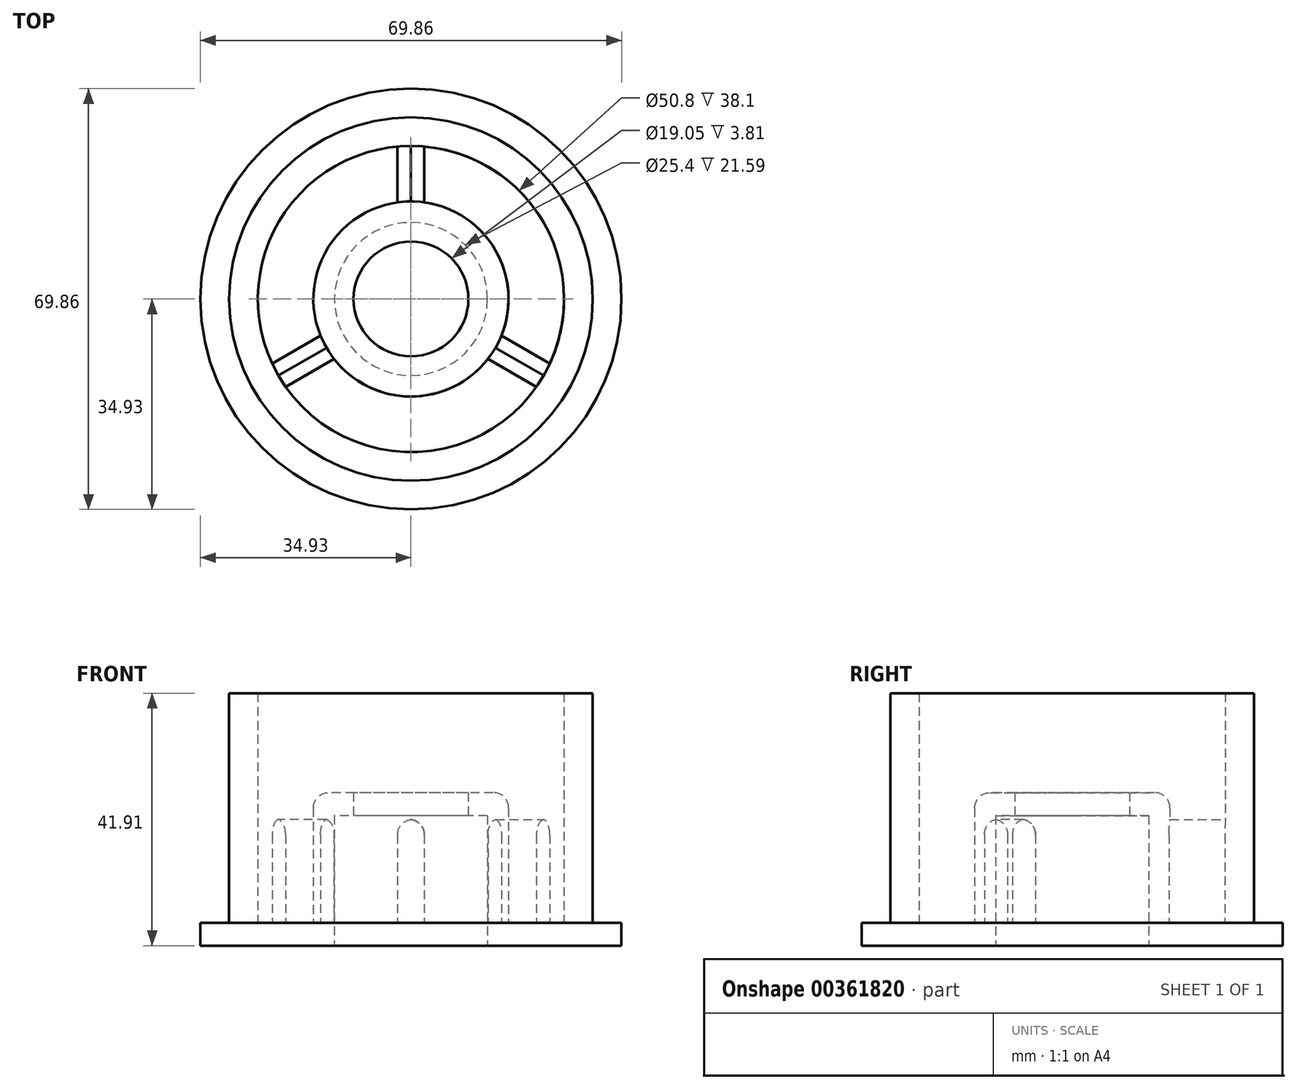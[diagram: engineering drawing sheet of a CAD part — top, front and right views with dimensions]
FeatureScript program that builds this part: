
annotation { "Feature Type Name" : "Feature", "Feature Type Description" : "" }
export const myFeature = defineFeature(function(context is Context, id is Id, definition is map)
    precondition{}
    {
        {
            var Q0;
            Q0=qCreatedBy(makeId("Top.planeOp"),FACE);
            var sketch = newSketch(context, id + "F0", { "sketchPlane" : qUnion([Q0])});
            skCircle(sketch, "E0", {"center": v(0, 0) * mm, "radius": 34.93 * mm});
            skCircle(sketch, "E1", {"center": v(0, 0) * mm, "radius": 30.16 * mm});
            skCircle(sketch, "E2", {"center": v(0, 0) * mm, "radius": 25.4 * mm});
            skCircle(sketch, "E3", {"center": v(0, 0) * mm, "radius": 16.2 * mm});
            skCircle(sketch, "E4", {"center": v(0, 0) * mm, "radius": 9.53 * mm});
            skCircle(sketch, "E5", {"center": v(0, 0) * mm, "radius": 12.7 * mm});
            skLineSegment(sketch, "E6.left", {"start": v(2.22, 16.04) * mm, "end": v(2.22, 25.3) * mm});
            skLineSegment(sketch, "E6.right", {"start": v(-2.22, 16.04) * mm, "end": v(-2.22, 25.3) * mm});
            skPoint(sketch, "E6.middle", {"position": v(0, 20.67) * mm});
            skPoint(sketch, "E7.1.0", {"position": v(-17.9, -10.34) * mm});
            skLineSegment(sketch, "E7.1.1", {"start": v(-12.78, -9.94) * mm, "end": v(-20.8, -14.58) * mm});
            skLineSegment(sketch, "E7.1.2", {"start": v(-15, -6.1) * mm, "end": v(-23.02, -10.73) * mm});
            skPoint(sketch, "E7.2.0", {"position": v(17.9, -10.34) * mm});
            skLineSegment(sketch, "E7.2.1", {"start": v(15, -6.1) * mm, "end": v(23.02, -10.73) * mm});
            skLineSegment(sketch, "E7.2.2", {"start": v(12.78, -9.94) * mm, "end": v(20.8, -14.58) * mm});
            skSolve(sketch);
        }
        {
            var Q0;
            Q0=makeQuery(id+"F0.imprint","IMPRINT",FACE,{"disambiguationData":[TD([[makeQuery(id+"F0.imprint","IMPRINT",EDGE,{"derivedFrom":sQuery(id+"F0.wireOp",EDGE,"E0")}),1.0]])]});
            extrude(context, id + "F1", {"entities" : qUnion([Q0]), "depth" : 3.8 * mm});
        }
        {
            var Q0;
            Q0=makeQuery(id+"F0.imprint","IMPRINT",FACE,{"disambiguationData":[TD([[makeQuery(id+"F0.imprint","IMPRINT",EDGE,{"derivedFrom":sQuery(id+"F0.wireOp",EDGE,"E1")}),1.0]])]});
            extrude(context, id + "F2", {"entities" : qUnion([Q0]), "operationType" : NewBodyOperationType.ADD, "depth" : 41.9 * mm});
        }
        {
            var Q0;
            {var subQ0=sQuery(id+"F0.wireOp",EDGE,"E6.left");Q0=makeQuery(id+"F0.imprint","IMPRINT",FACE,{"disambiguationData":[TD([[makeQuery(id+"F0.imprint","IMPRINT",EDGE,{"derivedFrom":subQ0}),-1.0]])]});}
            var Q1;
            {var subQ0=sQuery(id+"F0.wireOp",EDGE,"E6.right");Q1=makeQuery(id+"F0.imprint","IMPRINT",FACE,{"disambiguationData":[TD([[makeQuery(id+"F0.imprint","IMPRINT",EDGE,{"derivedFrom":subQ0}),1.0]])]});}
            var Q2;
            {var subQ0=sQuery(id+"F0.wireOp",EDGE,"E7.1.1");Q2=makeQuery(id+"F0.imprint","IMPRINT",FACE,{"disambiguationData":[TD([[makeQuery(id+"F0.imprint","IMPRINT",EDGE,{"derivedFrom":subQ0}),1.0]])]});}
            extrude(context, id + "F3", {"entities" : qUnion([Q0, Q1, Q2]), "operationType" : NewBodyOperationType.ADD, "depth" : 3.8 * mm, "offsetDistance" : 25.4 * mm});
        }
        {
            var Q0;
            {var subQ0=sQuery(id+"F0.wireOp",EDGE,"E6.left");Q0=makeQuery(id+"F0.imprint","IMPRINT",FACE,{"disambiguationData":[TD([[makeQuery(id+"F0.imprint","IMPRINT",EDGE,{"derivedFrom":subQ0}),1.0]])]});}
            var Q1;
            {var subQ0=sQuery(id+"F0.wireOp",EDGE,"E7.2.1");Q1=makeQuery(id+"F0.imprint","IMPRINT",FACE,{"disambiguationData":[TD([[makeQuery(id+"F0.imprint","IMPRINT",EDGE,{"derivedFrom":subQ0}),-1.0]])]});}
            var Q2;
            {var subQ0=sQuery(id+"F0.wireOp",EDGE,"E7.1.1");Q2=makeQuery(id+"F0.imprint","IMPRINT",FACE,{"disambiguationData":[TD([[makeQuery(id+"F0.imprint","IMPRINT",EDGE,{"derivedFrom":subQ0}),-1.0]])]});}
            extrude(context, id + "F4", {"entities" : qUnion([Q0, Q1, Q2]), "operationType" : NewBodyOperationType.ADD, "depth" : 20.95 * mm, "offsetDistance" : 25.4 * mm});
        }
        {
            var Q0;
            Q0=makeQuery(id+"F0.imprint","IMPRINT",FACE,{"disambiguationData":[TD([[makeQuery(id+"F0.imprint","IMPRINT",EDGE,{"derivedFrom":sQuery(id+"F0.wireOp",EDGE,"E5")}),-1.0]])]});
            extrude(context, id + "F5", {"entities" : qUnion([Q0]), "operationType" : NewBodyOperationType.ADD, "depth" : 25.4 * mm});
        }
        {
            var Q0;
            Q0=makeQuery(id+"F0.imprint","IMPRINT",FACE,{"disambiguationData":[TD([[makeQuery(id+"F0.imprint","IMPRINT",EDGE,{"derivedFrom":sQuery(id+"F0.wireOp",EDGE,"E4")}),-1.0]])]});
            extrude(context, id + "F6", {"entities" : qUnion([Q0]), "operationType" : NewBodyOperationType.ADD, "depth" : 25.4 * mm, "offsetDistance" : 25.4 * mm});
        }
        {
            var Q0;
            Q0=makeQuery(id+"F0.imprint","IMPRINT",FACE,{"disambiguationData":[TD([[makeQuery(id+"F0.imprint","IMPRINT",EDGE,{"derivedFrom":sQuery(id+"F0.wireOp",EDGE,"E4")}),-1.0]])]});
            extrude(context, id + "F7", {"entities" : qUnion([Q0]), "operationType" : NewBodyOperationType.REMOVE, "depth" : 21.59 * mm});
        }
        {
            var Q0;
            Q0=makeQuery(id+"F5.opExtrude","CAP_EDGE",EDGE,{"disambiguationData":[OSD([sQuery(id+"F0.wireOp",EDGE,"E3")])],"isStart":false});
            var Q1;
            Q1=makeQuery(id+"F4.opExtrude","CAP_EDGE",EDGE,{"disambiguationData":[OSD([sQuery(id+"F0.wireOp",EDGE,"E6.right")])],"isStart":false});
            var Q2;
            Q2=makeQuery(id+"F4.opExtrude","CAP_EDGE",EDGE,{"disambiguationData":[OSD([sQuery(id+"F0.wireOp",EDGE,"E6.left")])],"isStart":false});
            var Q3;
            Q3=makeQuery(id+"F4.opExtrude","CAP_EDGE",EDGE,{"disambiguationData":[OSD([sQuery(id+"F0.wireOp",EDGE,"E7.1.1")])],"isStart":false});
            var Q4;
            Q4=makeQuery(id+"F4.opExtrude","CAP_EDGE",EDGE,{"disambiguationData":[OSD([sQuery(id+"F0.wireOp",EDGE,"E7.1.2")])],"isStart":false});
            var Q5;
            Q5=makeQuery(id+"F4.opExtrude","CAP_EDGE",EDGE,{"disambiguationData":[OSD([sQuery(id+"F0.wireOp",EDGE,"E7.2.1")])],"isStart":false});
            var Q6;
            Q6=makeQuery(id+"F4.opExtrude","CAP_EDGE",EDGE,{"disambiguationData":[OSD([sQuery(id+"F0.wireOp",EDGE,"E7.2.2")])],"isStart":false});
            fillet(context, id + "F8", {"entities" : qUnion([Q0, Q1, Q2, Q3, Q4, Q5, Q6]), "radius" : 2.54 * mm, "tangentPropagation" : true, "allowEdgeOverflow" : false});
        }
    });
